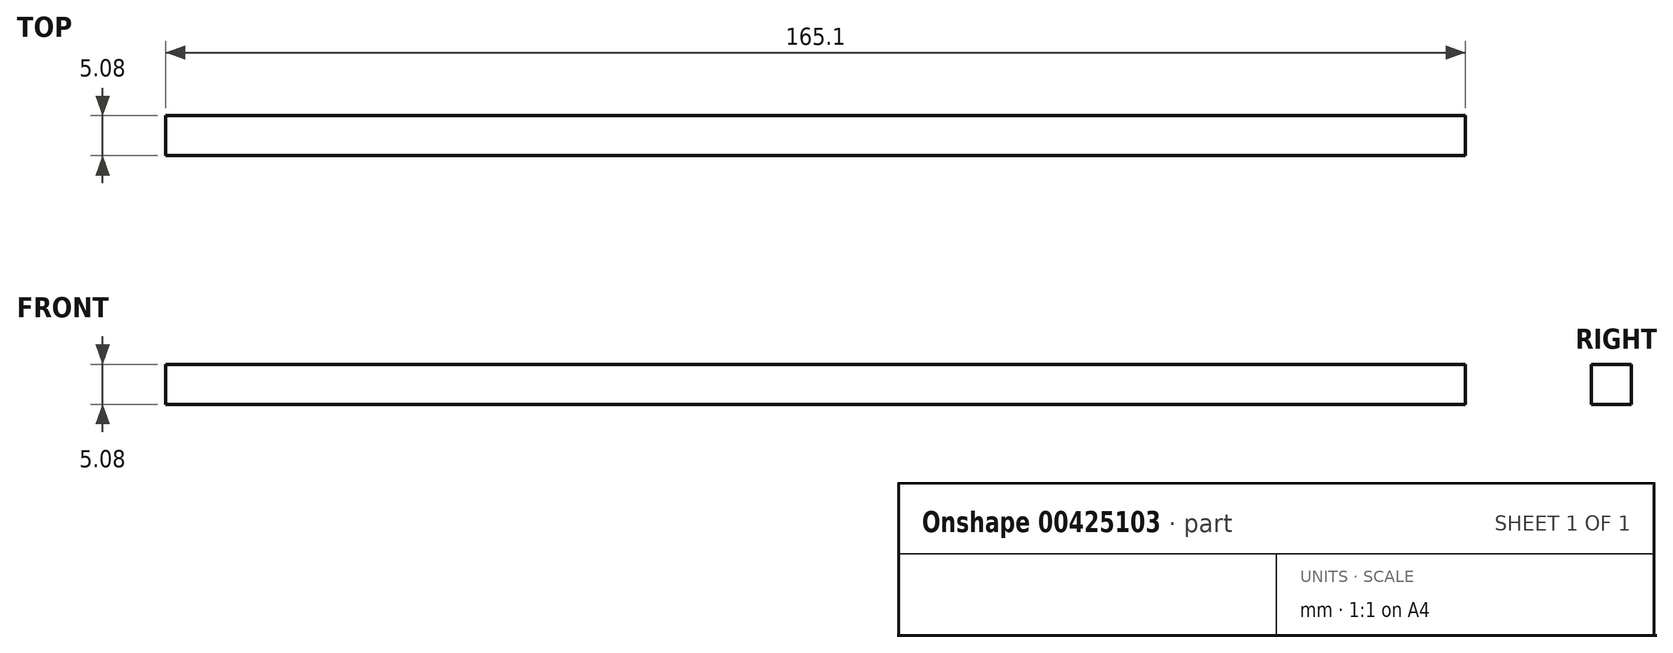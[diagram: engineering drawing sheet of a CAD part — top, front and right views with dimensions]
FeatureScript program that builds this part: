
annotation { "Feature Type Name" : "Feature", "Feature Type Description" : "" }
export const myFeature = defineFeature(function(context is Context, id is Id, definition is map)
    precondition{}
    {
        {
            var Q0;
            Q0=qCreatedBy(makeId("Front.planeOp"),FACE);
            var sketch = newSketch(context, id + "F0", { "sketchPlane" : qUnion([Q0])});
            skLineSegment(sketch, "E0.bottom", {"start": v(-100.31, -41.57) * mm, "end": v(64.79, -41.57) * mm});
            skLineSegment(sketch, "E0.top", {"start": v(-100.31, -46.65) * mm, "end": v(64.79, -46.65) * mm});
            skLineSegment(sketch, "E0.left", {"start": v(-100.31, -41.57) * mm, "end": v(-100.31, -46.65) * mm});
            skLineSegment(sketch, "E0.right", {"start": v(64.79, -41.57) * mm, "end": v(64.79, -46.65) * mm});
            skSolve(sketch);
        }
        {
            var Q0;
            Q0 = qSketchRegion(id + "F0", true);
            extrude(context, id + "F1", {"entities" : qUnion([Q0]), "depth" : 5.08 * mm});
        }
    });
